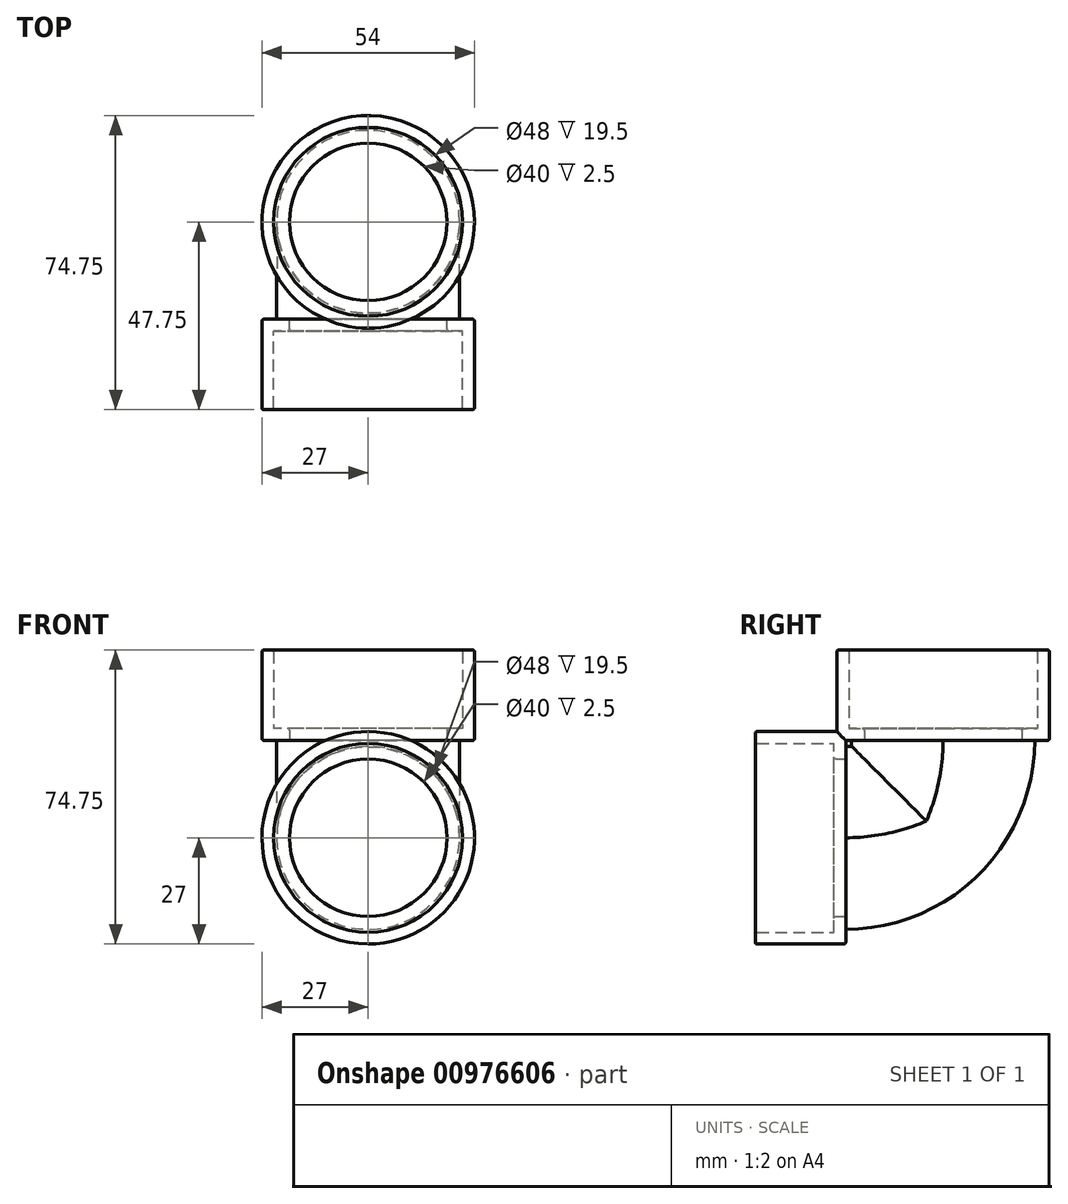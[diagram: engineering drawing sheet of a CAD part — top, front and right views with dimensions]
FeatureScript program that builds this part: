
annotation { "Feature Type Name" : "Feature", "Feature Type Description" : "" }
export const myFeature = defineFeature(function(context is Context, id is Id, definition is map)
    precondition{}
    {
        {
            var Q0;
            Q0=qCreatedBy(makeId("Right.planeOp"),FACE);
            var sketch = newSketch(context, id + "F0", { "sketchPlane" : qUnion([Q0])});
            skLineSegment(sketch, "E0.bottom", {"start": v(-22.5, 23.25) * mm, "end": v(-24, 23.25) * mm});
            skLineSegment(sketch, "E0.right", {"start": v(-24, 23.25) * mm, "end": v(-24, -23.25) * mm});
            skPoint(sketch, "E0.middle", {"position": v(0, 0) * mm});
            skLineSegment(sketch, "E1.top", {"start": v(24, 24.75) * mm, "end": v(-22.5, 24.75) * mm});
            skLineSegment(sketch, "E1.left", {"start": v(24, 23.25) * mm, "end": v(24, 24.75) * mm});
            skLineSegment(sketch, "E1.right", {"start": v(-22.5, 23.25) * mm, "end": v(-22.5, 24.75) * mm});
            skArc(sketch, "E2", {"start": v(-24, -23.25) * mm, "mid": v(9.94, -9.2) * mm, "end": v(24, 24.75) * mm});
            skPoint(sketch, "E1.bottom.start.orphan", {"position": v(24, -23.25) * mm});
            skSolve(sketch);
        }
        {
            var Q0;
            Q0=makeQuery(id+"F0.imprint","IMPRINT",FACE,{"disambiguationData":[TD([[makeQuery(id+"F0.imprint","IMPRINT",EDGE,{"derivedFrom":sQuery(id+"F0.wireOp",EDGE,"E0.bottom")}),1.0]])]});
            extrude(context, id + "F1", {"entities" : qUnion([Q0]), "depth" : 46.5 * mm, "offsetDistance" : 25 * mm});
        }
        {
            var Q0;
            Q0=makeQuery(id+"F1.opExtrude","CAP_EDGE",EDGE,{"disambiguationData":[OSD([sQuery(id+"F0.wireOp",EDGE,"E1.right")])],"isStart":false});
            var Q1;
            Q1=makeQuery(id+"F1.opExtrude","CAP_EDGE",EDGE,{"disambiguationData":[OSD([sQuery(id+"F0.wireOp",EDGE,"E0.bottom")])],"isStart":false});
            var Q2;
            Q2=makeQuery(id+"F1.opExtrude","CAP_EDGE",EDGE,{"disambiguationData":[OSD([sQuery(id+"F0.wireOp",EDGE,"E0.bottom")])],"isStart":true});
            var Q3;
            Q3=makeQuery(id+"F1.opExtrude","CAP_EDGE",EDGE,{"disambiguationData":[OSD([sQuery(id+"F0.wireOp",EDGE,"E1.right")])],"isStart":true});
            var Q4;
            Q4=makeQuery(id+"F1.opExtrude","CAP_EDGE",EDGE,{"disambiguationData":[OSD([sQuery(id+"F0.wireOp",EDGE,"E0.top"),sQuery(id+"F0.wireOp",EDGE,"E1.bottom")])],"isStart":true});
            var Q5;
            Q5=makeQuery(id+"F1.opExtrude","CAP_EDGE",EDGE,{"disambiguationData":[OSD([sQuery(id+"F0.wireOp",EDGE,"E1.left")])],"isStart":true});
            var Q6;
            Q6=makeQuery(id+"F1.opExtrude","CAP_EDGE",EDGE,{"disambiguationData":[OSD([sQuery(id+"F0.wireOp",EDGE,"E1.left")])],"isStart":false});
            var Q7;
            Q7=makeQuery(id+"F1.opExtrude","CAP_EDGE",EDGE,{"disambiguationData":[OSD([sQuery(id+"F0.wireOp",EDGE,"E0.top"),sQuery(id+"F0.wireOp",EDGE,"E1.bottom")])],"isStart":false});
            var Q8;
            Q8=makeQuery(id+"F1.opExtrude","CAP_EDGE",EDGE,{"disambiguationData":[OSD([sQuery(id+"F0.wireOp",EDGE,"E2")])],"isStart":false});
            var Q9;
            Q9=makeQuery(id+"F1.opExtrude","CAP_EDGE",EDGE,{"disambiguationData":[OSD([sQuery(id+"F0.wireOp",EDGE,"E2")])],"isStart":true});
            fillet(context, id + "F2", {"entities" : qUnion([Q0, Q1, Q2, Q3, Q4, Q5, Q6, Q7, Q8, Q9]), "radius" : 23.25 * mm, "tangentPropagation" : true, "allowEdgeOverflow" : false});
        }
        {
            var Q0;
            Q0=makeQuery(id+"F1.opExtrude","SWEPT_FACE",FACE,{"disambiguationData":[OSD([sQuery(id+"F0.wireOp",EDGE,"E1.top")])]});
            var sketch = newSketch(context, id + "F3", { "sketchPlane" : qUnion([Q0])});
            skCircle(sketch, "E3", {"center": v(23.25, 0.75) * mm, "radius": 27 * mm});
            skCircle(sketch, "E4", {"center": v(23.25, 0.75) * mm, "radius": 24 * mm});
            skCircle(sketch, "E5", {"center": v(23.25, 0.75) * mm, "radius": 20 * mm});
            skSolve(sketch);
        }
        {
            var Q0;
            Q0=makeQuery(id+"F1.opExtrude","SWEPT_FACE",FACE,{"disambiguationData":[OSD([sQuery(id+"F0.wireOp",EDGE,"E0.right")])]});
            var sketch = newSketch(context, id + "F4", { "sketchPlane" : qUnion([Q0])});
            skCircle(sketch, "E6", {"center": v(23.25, 0) * mm, "radius": 27 * mm});
            skCircle(sketch, "E7", {"center": v(23.25, 0) * mm, "radius": 24 * mm});
            skCircle(sketch, "E8", {"center": v(23.25, 0) * mm, "radius": 20 * mm});
            skSolve(sketch);
        }
        {
            var Q0;
            Q0=makeQuery(id+"F3.imprint","IMPRINT",FACE,{"disambiguationData":[TD([[makeQuery(id+"F3.imprint","IMPRINT",EDGE,{"derivedFrom":sQuery(id+"F3.wireOp",EDGE,"E5")}),-1.0]])]});
            var Q1;
            Q1=makeQuery(id+"F3.imprint","IMPRINT",FACE,{"disambiguationData":[TD([[makeQuery(id+"F3.imprint","IMPRINT",EDGE,{"derivedFrom":sQuery(id+"F3.wireOp",EDGE,"E4")}),1.0]])]});
            extrude(context, id + "F5", {"entities" : qUnion([Q0, Q1]), "operationType" : NewBodyOperationType.ADD, "depth" : 3 * mm, "offsetDistance" : 25 * mm});
        }
        {
            var Q0;
            Q0=makeQuery(id+"F3.imprint","IMPRINT",FACE,{"disambiguationData":[TD([[makeQuery(id+"F3.imprint","IMPRINT",EDGE,{"derivedFrom":sQuery(id+"F3.wireOp",EDGE,"E3")}),1.0]])]});
            extrude(context, id + "F6", {"entities" : qUnion([Q0]), "operationType" : NewBodyOperationType.ADD, "depth" : 23 * mm, "offsetDistance" : 25 * mm});
        }
        {
            var Q0;
            Q0=makeQuery(id+"F4.imprint","IMPRINT",FACE,{"disambiguationData":[TD([[makeQuery(id+"F4.imprint","IMPRINT",EDGE,{"derivedFrom":sQuery(id+"F4.wireOp",EDGE,"E8")}),-1.0]])]});
            var Q1;
            Q1=makeQuery(id+"F4.imprint","IMPRINT",FACE,{"disambiguationData":[TD([[makeQuery(id+"F4.imprint","IMPRINT",EDGE,{"derivedFrom":sQuery(id+"F4.wireOp",EDGE,"E7")}),1.0]])]});
            extrude(context, id + "F7", {"entities" : qUnion([Q0, Q1]), "operationType" : NewBodyOperationType.ADD, "depth" : 3 * mm, "offsetDistance" : 25 * mm});
        }
        {
            var Q0;
            Q0=makeQuery(id+"F4.imprint","IMPRINT",FACE,{"disambiguationData":[TD([[makeQuery(id+"F4.imprint","IMPRINT",EDGE,{"derivedFrom":sQuery(id+"F4.wireOp",EDGE,"E6")}),1.0]])]});
            extrude(context, id + "F8", {"entities" : qUnion([Q0]), "operationType" : NewBodyOperationType.ADD, "depth" : 23 * mm, "offsetDistance" : 25 * mm});
        }
        {
            var Q0;
            Q0=makeQuery(id+"F8.opExtrude","CAP_EDGE",EDGE,{"disambiguationData":[OSD([sQuery(id+"F4.wireOp",EDGE,"E6")])],"isStart":true});
            var Q1;
            Q1=makeQuery(id+"F6.opExtrude","CAP_EDGE",EDGE,{"disambiguationData":[OSD([sQuery(id+"F3.wireOp",EDGE,"E3")])],"isStart":true});
            var Q2;
            Q2=makeQuery(id+"F8.opExtrude","CAP_FACE",FACE,{"disambiguationData":[OSD([sQuery(id+"F4.wireOp",EDGE,"E6"),sQuery(id+"F4.wireOp",EDGE,"E7")])],"isStart":false});
            var Q3;
            Q3=makeQuery(id+"F6.opExtrude","CAP_FACE",FACE,{"disambiguationData":[OSD([sQuery(id+"F3.wireOp",EDGE,"E3"),sQuery(id+"F3.wireOp",EDGE,"E4")])],"isStart":false});
            var Q4;
            Q4=makeQuery(id+"F5.opExtrude","CAP_EDGE",EDGE,{"disambiguationData":[OSD([sQuery(id+"F3.wireOp",EDGE,"E4")])],"isStart":false});
            var Q5;
            Q5=makeQuery(id+"F5.opExtrude","CAP_EDGE",EDGE,{"disambiguationData":[OSD([sQuery(id+"F3.wireOp",EDGE,"E5")])],"isStart":false});
            var Q6;
            Q6=makeQuery(id+"F7.opExtrude","CAP_EDGE",EDGE,{"disambiguationData":[OSD([sQuery(id+"F4.wireOp",EDGE,"E8")])],"isStart":false});
            var Q7;
            Q7=makeQuery(id+"F7.opExtrude","CAP_EDGE",EDGE,{"disambiguationData":[OSD([sQuery(id+"F4.wireOp",EDGE,"E7")])],"isStart":false});
            fillet(context, id + "F9", {"entities" : qUnion([Q0, Q1, Q2, Q3, Q4, Q5, Q6, Q7]), "radius" : .5 * mm, "tangentPropagation" : true, "allowEdgeOverflow" : false});
        }
    });
